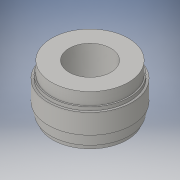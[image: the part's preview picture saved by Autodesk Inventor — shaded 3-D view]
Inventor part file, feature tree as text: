
AUTODESK INVENTOR PART (.ipt)
format: ipt  version: 2016 (Build 200138000, 138)  size: 144,384 bytes
history: native  units: mm
features: other x3, sketch x2
ambient origin geometry x8: Origin, YZ Plane, XZ Plane, XY Plane, X Axis, Y Axis, Z Axis, Center Point
bodies: Solid1 (feature_tree)
feature tree (5):
  other  "50mm_1_4G_body_disassembled.ipt"
  other  "Solid1::50mm_1_4G_body_disassembled.ipt"
  other  "TaggingFeature1"
  sketch  "Sketch1"  dims[d0=10.0mm]
  sketch  "Sketch4"
